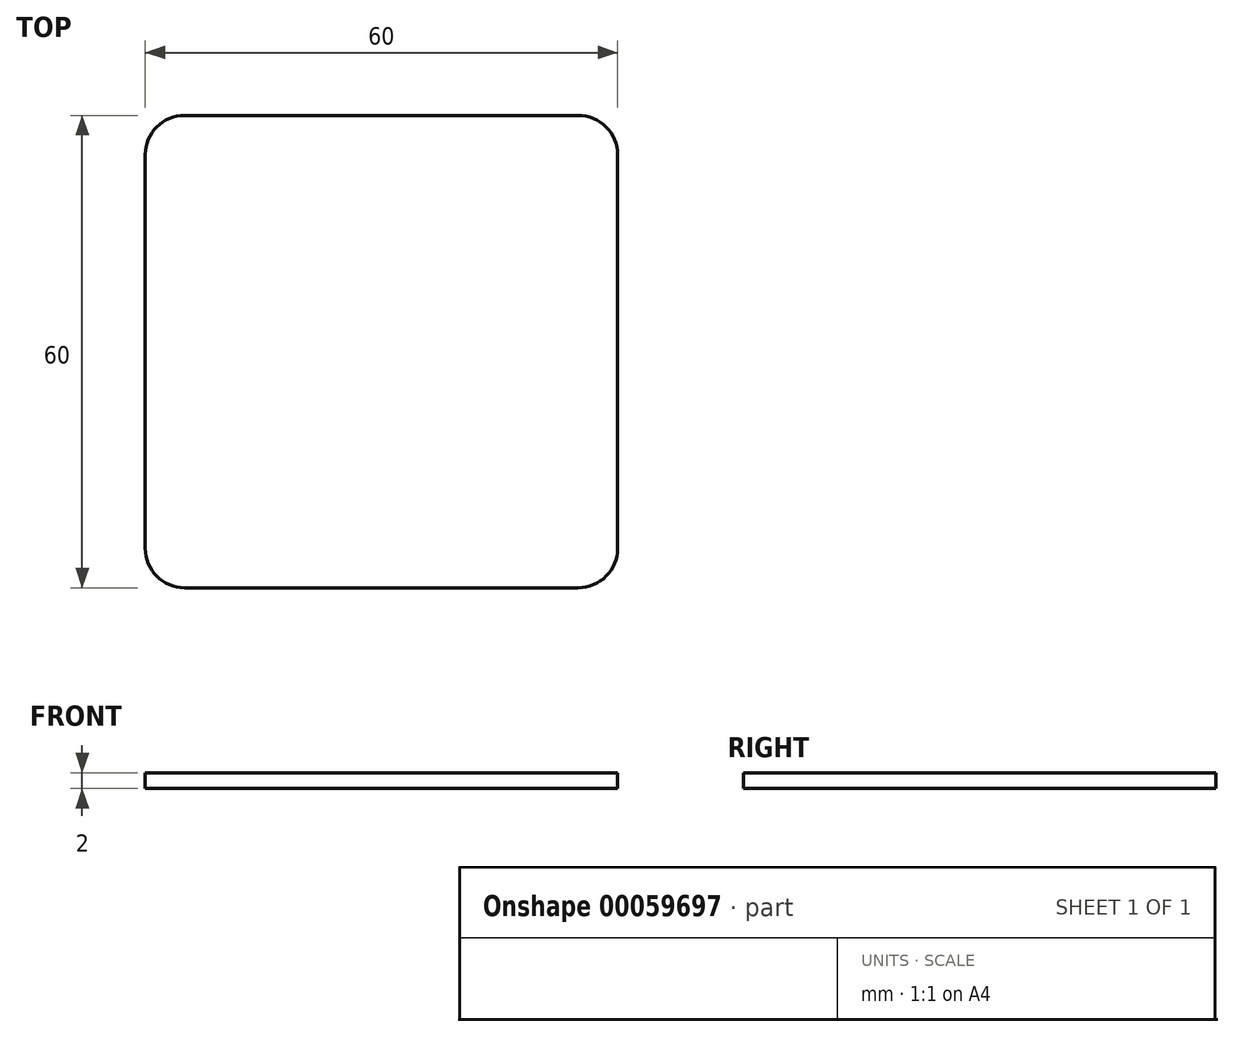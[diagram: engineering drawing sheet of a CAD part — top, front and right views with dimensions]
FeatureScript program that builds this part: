
annotation { "Feature Type Name" : "Feature", "Feature Type Description" : "" }
export const myFeature = defineFeature(function(context is Context, id is Id, definition is map)
    precondition{}
    {
        {
            var Q0;
            Q0=qCreatedBy(makeId("Top.planeOp"),FACE);
            var sketch = newSketch(context, id + "F0", { "sketchPlane" : qUnion([Q0])});
            skLineSegment(sketch, "E0.bottom", {"start": v(0, 0) * mm, "end": v(60, 0) * mm});
            skLineSegment(sketch, "E0.top", {"start": v(0, -60) * mm, "end": v(60, -60) * mm});
            skLineSegment(sketch, "E0.left", {"start": v(0, 0) * mm, "end": v(0, -60) * mm});
            skLineSegment(sketch, "E0.right", {"start": v(60, 0) * mm, "end": v(60, -60) * mm});
            skSolve(sketch);
        }
        {
            var Q0;
            Q0 = qSketchRegion(id + "F0", true);
            extrude(context, id + "F1", {"entities" : qUnion([Q0]), "depth" : 2 * mm});
        }
        {
            var Q0;
            Q0=makeQuery(id+"F1.opExtrude","SWEPT_EDGE",EDGE,{"disambiguationData":[OSD([sQuery(id+"F0.wireOp",EDGE,"E0.bottom"),sQuery(id+"F0.wireOp",EDGE,"E0.right")])]});
            var Q1;
            Q1=makeQuery(id+"F1.opExtrude","SWEPT_EDGE",EDGE,{"disambiguationData":[OSD([sQuery(id+"F0.wireOp",EDGE,"E0.top"),sQuery(id+"F0.wireOp",EDGE,"E0.right")])]});
            var Q2;
            Q2=makeQuery(id+"F1.opExtrude","SWEPT_EDGE",EDGE,{"disambiguationData":[OSD([sQuery(id+"F0.wireOp",EDGE,"E0.top"),sQuery(id+"F0.wireOp",EDGE,"E0.left")])]});
            var Q3;
            Q3=makeQuery(id+"F1.opExtrude","SWEPT_EDGE",EDGE,{"disambiguationData":[OSD([sQuery(id+"F0.wireOp",EDGE,"E0.bottom"),sQuery(id+"F0.wireOp",EDGE,"E0.left")])]});
            fillet(context, id + "F2", {"entities" : qUnion([Q0, Q1, Q2, Q3]), "radius" : 5 * mm, "tangentPropagation" : true, "allowEdgeOverflow" : false});
        }
    });
